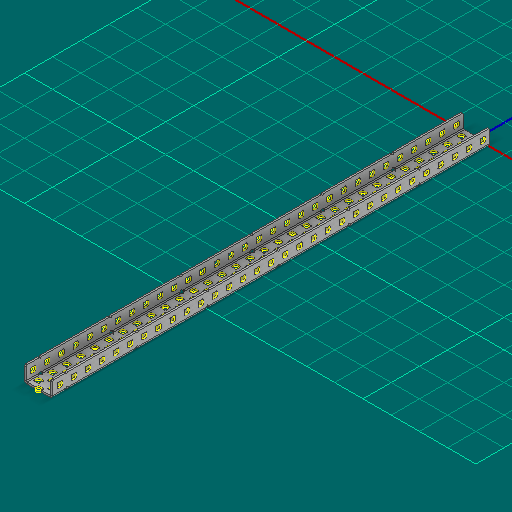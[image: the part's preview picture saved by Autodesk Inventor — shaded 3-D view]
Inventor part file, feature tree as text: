
AUTODESK INVENTOR PART (.ipt)
format: ipt  version: 2025 (Build 290162000, 162)  size: 2,585,600 bytes
history: native  units: in
note: dims shown in document units (in); Inventor stores cm internally (conversion verified against a paired STEP export)
features: other x316, sketch x5, sheet_metal_op x1
ambient origin geometry x8: Origin, YZ Plane, XZ Plane, XY Plane, X Axis, Y Axis, Z Axis, Center Point
bodies: Solid1 (feature_tree)
feature tree (322):
  other  "Alu C 1x2x1x31.ipt"
  other  "Solid1::Alu C 1x2x1x31.ipt"
  other  "TaggingFeature1"
  sketch  "Sketch1"  dims[d0=0.3937in]
  sketch  "Sketch2"  dims[d1=0.0625in]
  sketch  "Sketch3"
  other  "Flange Pattern Sketch"
  sketch  "Sketch9"
  sheet_metal_op  "Body Pattern Sketch"
  other  "Arc Length"
  sketch  "Sketch14"
  other  "Flange Pattern Plane"
  other  "Srf1"
  other  "Srf2"
  other  "Srf3"
  other  "Srf4"
  other  "Srf5"
  other  "Srf6"
  other  "Srf7"
  other  "Srf8"
  other  "Srf9"
  other  "Srf10"
  other  "Srf11"
  other  "Srf12"
  other  "Srf13"
  other  "Srf14"
  other  "Srf15"
  other  "Srf16"
  other  "Srf17"
  other  "Srf18"
  other  "Srf19"
  other  "Srf20"
  other  "Srf21"
  other  "Srf22"
  other  "Srf23"
  other  "Srf24"
  other  "Srf25"
  other  "Srf26"
  other  "Srf27"
  other  "Srf28"
  other  "Srf29"
  other  "Srf30"
  other  "Srf31"
  other  "Srf32"
  other  "Srf33"
  other  "Srf34"
  other  "Srf35"
  other  "Srf36"
  other  "Srf37"
  other  "Srf38"
  other  "Srf39"
  other  "Srf40"
  other  "Srf41"
  other  "Srf42"
  other  "Srf43"
  other  "Srf44"
  other  "Srf45"
  other  "Srf46"
  other  "Srf47"
  other  "Srf48"
  other  "Srf49"
  other  "Srf50"
  other  "Srf51"
  other  "Srf52"
  other  "Srf53"
  other  "Srf54"
  other  "Srf55"
  other  "Srf56"
  other  "Srf57"
  other  "Srf58"
  other  "Srf59"
  other  "Srf60"
  other  "Srf61"
  other  "Srf62"
  other  "Srf63"
  other  "Srf64"
  other  "Srf65"
  other  "Srf66"
  other  "Srf67"
  other  "Srf68"
  other  "Srf69"
  other  "Srf70"
  other  "Srf71"
  other  "Srf72"
  other  "Srf73"
  other  "Srf74"
  other  "Srf75"
  other  "Srf76"
  other  "Srf77"
  other  "Srf78"
  other  "Srf79"
  other  "Srf80"
  other  "Srf81"
  other  "Srf82"
  other  "Srf83"
  other  "Srf84"
  other  "Srf85"
  other  "Srf86"
  other  "Srf87"
  other  "Srf88"
  other  "Srf89"
  other  "Srf90"
  other  "Srf91"
  other  "Srf92"
  other  "Srf93"
  other  "Srf94"
  other  "Srf95"
  other  "Srf96"
  other  "Srf97"
  other  "Srf98"
  other  "Srf99"
  other  "Srf100"
  other  "Srf101"
  other  "Srf102"
  other  "Srf103"
  other  "Srf104"
  other  "Srf105"
  other  "Srf106"
  other  "Srf107"
  other  "Srf108"
  other  "Srf109"
  other  "Srf110"
  other  "Srf111"
  other  "Srf112"
  other  "Srf113"
  other  "Srf114"
  other  "Srf115"
  other  "Srf116"
  other  "Srf117"
  other  "Srf118"
  other  "Srf119"
  other  "Srf120"
  other  "Srf121"
  other  "Srf122"
  other  "Srf123"
  other  "Srf124"
  other  "Srf125"
  other  "Srf126"
  other  "Srf127"
  other  "Srf128"
  other  "Srf129"
  other  "Srf130"
  other  "Srf131"
  other  "Srf132"
  other  "Srf133"
  other  "Srf134"
  other  "Srf135"
  other  "Srf136"
  other  "Srf137"
  other  "Srf138"
  other  "Srf139"
  other  "Srf140"
  other  "Srf141"
  other  "Srf142"
  other  "Srf143"
  other  "Srf144"
  other  "Srf145"
  other  "Srf146"
  other  "Srf147"
  other  "Srf148"
  other  "Srf149"
  other  "Srf150"
  other  "Srf151"
  other  "Srf152"
  other  "Srf153"
  other  "Srf154"
  other  "Srf155"
  other  "Srf1::Derived"
  other  "Srf2::Derived"
  other  "Srf823::Derived"
  other  "Srf824::Derived"
  other  "Srf825::Derived"
  other  "Srf826::Derived"
  other  "Srf827::Derived"
  other  "Srf828::Derived"
  other  "Srf829::Derived"
  other  "Srf922::Derived"
  other  "Srf923::Derived"
  other  "Srf924::Derived"
  other  "Srf925::Derived"
  other  "Srf926::Derived"
  other  "Srf1143::Derived"
  other  "Srf1144::Derived"
  other  "Srf1145::Derived"
  other  "Srf1146::Derived"
  other  "Srf1147::Derived"
  other  "Srf1148::Derived"
  other  "Srf1149::Derived"
  other  "Srf1150::Derived"
  other  "Srf1151::Derived"
  other  "Srf1152::Derived"
  other  "Srf1153::Derived"
  other  "Srf1154::Derived"
  other  "Srf1155::Derived"
  other  "Srf1156::Derived"
  other  "Srf1157::Derived"
  other  "Srf1158::Derived"
  other  "Srf1159::Derived"
  other  "Srf1160::Derived"
  other  "Srf1161::Derived"
  other  "Srf1162::Derived"
  other  "Srf1163::Derived"
  other  "Srf1164::Derived"
  other  "Srf1165::Derived"
  other  "Srf1166::Derived"
  other  "Srf1167::Derived"
  other  "Srf1168::Derived"
  other  "Srf1169::Derived"
  other  "Srf1170::Derived"
  other  "Srf1171::Derived"
  other  "Srf1172::Derived"
  other  "Srf1173::Derived"
  other  "Srf1174::Derived"
  other  "Srf1175::Derived"
  other  "Srf1176::Derived"
  other  "Srf1177::Derived"
  other  "Srf1178::Derived"
  other  "Srf1179::Derived"
  other  "Srf1180::Derived"
  other  "Srf1181::Derived"
  other  "Srf1182::Derived"
  other  "Srf1183::Derived"
  other  "Srf1184::Derived"
  other  "Srf1185::Derived"
  other  "Srf1186::Derived"
  other  "Srf1187::Derived"
  other  "Srf1188::Derived"
  other  "Srf1189::Derived"
  other  "Srf1190::Derived"
  other  "Srf91::Derived"
  other  "Srf92::Derived"
  other  "Srf856::Derived"
  other  "Srf857::Derived"
  other  "Srf858::Derived"
  other  "Srf859::Derived"
  other  "Srf860::Derived"
  other  "Srf861::Derived"
  other  "Srf862::Derived"
  other  "Srf959::Derived"
  other  "Srf960::Derived"
  other  "Srf961::Derived"
  other  "Srf962::Derived"
  other  "Srf963::Derived"
  other  "Srf1199::Derived"
  other  "Srf1200::Derived"
  other  "Srf1201::Derived"
  other  "Srf1202::Derived"
  other  "Srf1203::Derived"
  other  "Srf1204::Derived"
  other  "Srf1205::Derived"
  other  "Srf1206::Derived"
  other  "Srf1207::Derived"
  other  "Srf1208::Derived"
  other  "Srf1209::Derived"
  other  "Srf1210::Derived"
  other  "Srf1211::Derived"
  other  "Srf1212::Derived"
  other  "Srf1213::Derived"
  other  "Srf1214::Derived"
  other  "Srf1215::Derived"
  other  "Srf1216::Derived"
  other  "Srf1217::Derived"
  other  "Srf1218::Derived"
  other  "Srf1219::Derived"
  other  "Srf1220::Derived"
  other  "Srf1221::Derived"
  other  "Srf1222::Derived"
  other  "Srf1223::Derived"
  other  "Srf1224::Derived"
  other  "Srf1225::Derived"
  other  "Srf1226::Derived"
  other  "Srf1227::Derived"
  other  "Srf1228::Derived"
  other  "Srf1229::Derived"
  other  "Srf1230::Derived"
  other  "Srf1231::Derived"
  other  "Srf1232::Derived"
  other  "Srf1233::Derived"
  other  "Srf1234::Derived"
  other  "Srf1235::Derived"
  other  "Srf1236::Derived"
  other  "Srf1237::Derived"
  other  "Srf1238::Derived"
  other  "Srf1239::Derived"
  other  "Srf1240::Derived"
  other  "Srf1241::Derived"
  other  "Srf1242::Derived"
  other  "Srf1243::Derived"
  other  "Srf1244::Derived"
  other  "Srf1245::Derived"
  other  "Srf1246::Derived"
  other  "Srf786::Derived"
  other  "Srf889::Derived"
  other  "Srf890::Derived"
  other  "Srf891::Derived"
  other  "Srf892::Derived"
  other  "Srf893::Derived"
  other  "Srf894::Derived"
  other  "Srf895::Derived"
  other  "Srf896::Derived"
  other  "Srf996::Derived"
  other  "Srf997::Derived"
  other  "Srf998::Derived"
  other  "Srf999::Derived"
  other  "Srf1000::Derived"
  other  "Srf1255::Derived"
  other  "Srf1256::Derived"
  other  "Srf1257::Derived"
  other  "Srf1258::Derived"
  other  "Srf1259::Derived"
  other  "Srf1260::Derived"
  other  "Srf1261::Derived"
  other  "Srf1262::Derived"
  other  "Srf1263::Derived"
  other  "Srf1264::Derived"
  other  "Srf1265::Derived"
  other  "Srf1266::Derived"
  other  "Srf1267::Derived"
  other  "Srf1268::Derived"
  other  "Srf1269::Derived"
  other  "Srf1270::Derived"
  other  "Srf1271::Derived"
